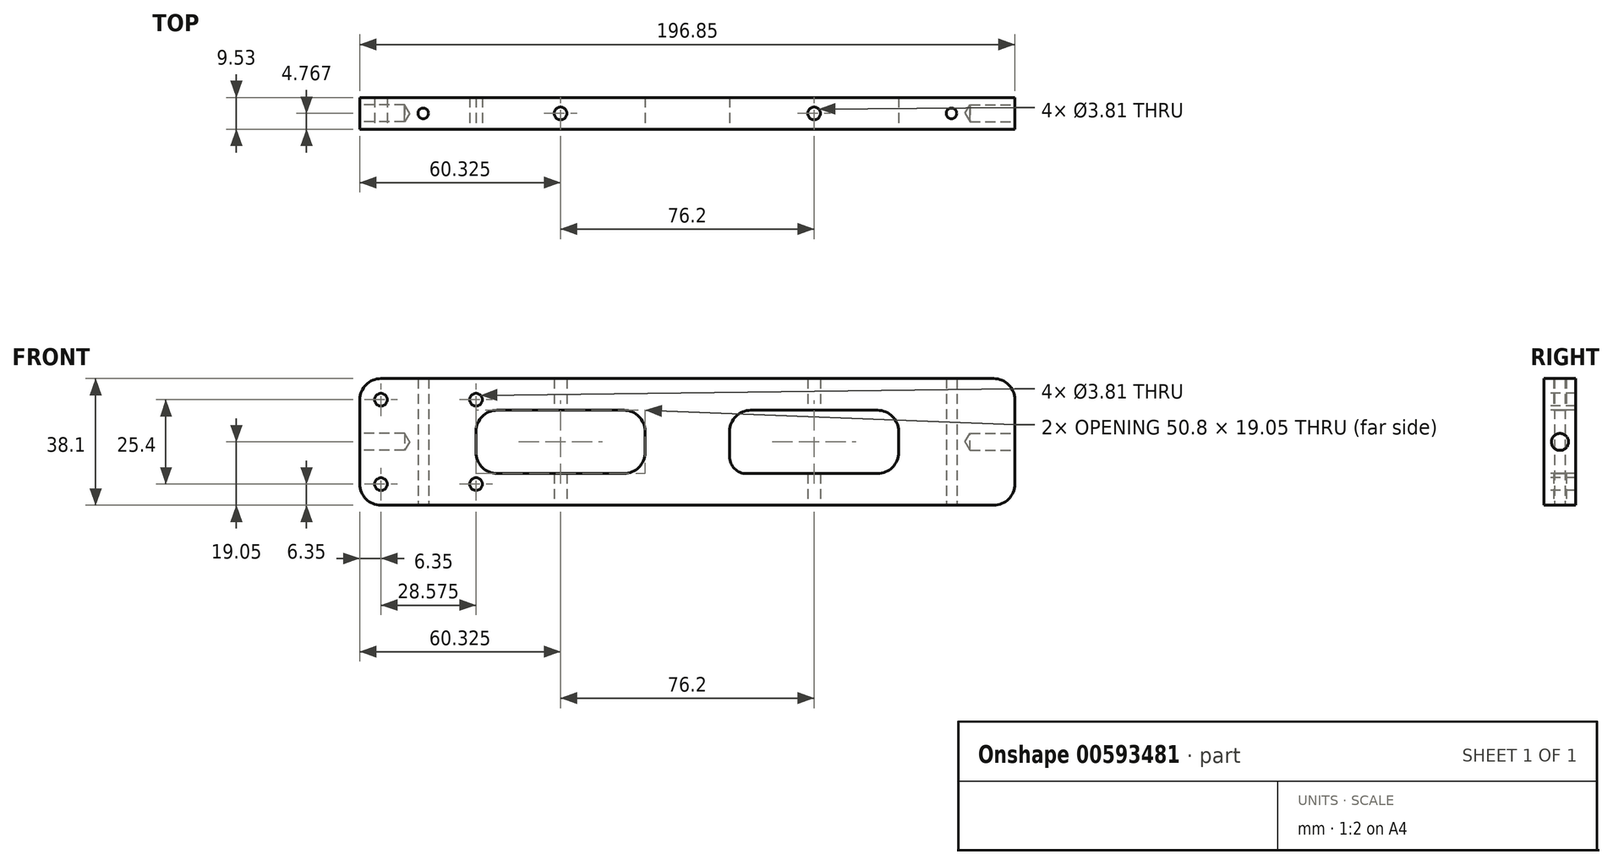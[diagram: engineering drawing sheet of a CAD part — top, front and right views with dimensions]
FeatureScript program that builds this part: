
annotation { "Feature Type Name" : "Feature", "Feature Type Description" : "" }
export const myFeature = defineFeature(function(context is Context, id is Id, definition is map)
    precondition{}
    {
        {
            var Q0;
            Q0=qCreatedBy(makeId("Front.planeOp"),FACE);
            var sketch = newSketch(context, id + "F0", { "sketchPlane" : qUnion([Q0])});
            skLineSegment(sketch, "E0.bottom", {"start": v(-196.85, 47.89) * mm, "end": v(0, 47.89) * mm});
            skLineSegment(sketch, "E0.top", {"start": v(-196.85, 9.79) * mm, "end": v(0, 9.79) * mm});
            skLineSegment(sketch, "E0.left", {"start": v(-196.85, 47.89) * mm, "end": v(-196.85, 9.79) * mm});
            skLineSegment(sketch, "E0.right", {"start": v(0, 47.89) * mm, "end": v(0, 9.79) * mm});
            skSolve(sketch);
        }
        {
            var Q0;
            Q0=makeQuery(id+"F0.imprint","IMPRINT",FACE,{"disambiguationData":[TD([[makeQuery(id+"F0.imprint","IMPRINT",EDGE,{"derivedFrom":sQuery(id+"F0.wireOp",EDGE,"E0.bottom")}),-1.0]])]});
            extrude(context, id + "F1", {"entities" : qUnion([Q0]), "depth" : 9.52 * mm, "offsetDistance" : 25.4 * mm});
        }
        {
            var Q0;
            Q0=makeQuery(id+"F1.opExtrude","SWEPT_EDGE",EDGE,{"disambiguationData":[OSD([sQuery(id+"F0.wireOp",EDGE,"E0.top"),sQuery(id+"F0.wireOp",EDGE,"E0.right")])]});
            fillet(context, id + "F2", {"entities" : qUnion([Q0]), "radius" : 6.35 * mm, "tangentPropagation" : true, "allowEdgeOverflow" : false});
        }
        {
            var Q0;
            Q0=makeQuery(id+"F1.opExtrude","SWEPT_EDGE",EDGE,{"disambiguationData":[OSD([sQuery(id+"F0.wireOp",EDGE,"E0.top"),sQuery(id+"F0.wireOp",EDGE,"E0.left")])]});
            fillet(context, id + "F3", {"entities" : qUnion([Q0]), "radius" : 6.35 * mm, "tangentPropagation" : true, "allowEdgeOverflow" : false});
        }
        {
            var Q0;
            Q0=makeQuery(id+"F1.opExtrude","CAP_FACE",FACE,{"disambiguationData":[OSD([sQuery(id+"F0.wireOp",EDGE,"E0.bottom"),sQuery(id+"F0.wireOp",EDGE,"E0.top"),sQuery(id+"F0.wireOp",EDGE,"E0.left"),sQuery(id+"F0.wireOp",EDGE,"E0.right")])],"isStart":false});
            var sketch = newSketch(context, id + "F4", { "sketchPlane" : qUnion([Q0])});
            skLineSegment(sketch, "E1.bottom", {"start": v(-161.93, 38.36) * mm, "end": v(-111.12, 38.36) * mm});
            skLineSegment(sketch, "E1.top", {"start": v(-161.93, 19.31) * mm, "end": v(-111.12, 19.31) * mm});
            skLineSegment(sketch, "E1.left", {"start": v(-161.93, 38.36) * mm, "end": v(-161.93, 19.31) * mm});
            skLineSegment(sketch, "E1.right", {"start": v(-111.12, 38.36) * mm, "end": v(-111.12, 19.31) * mm});
            skSolve(sketch);
        }
        {
            var Q0;
            Q0 = qSketchRegion(id + "F4", true);
            extrude(context, id + "F5", {"entities" : qUnion([Q0]), "operationType" : NewBodyOperationType.REMOVE, "oppositeDirection" : true, "depth" : 25.4 * mm, "offsetDistance" : 25.4 * mm});
        }
        {
            var Q0;
            Q0=makeQuery(id+"F5.boolean.opBoolean","COPY",EDGE,{"derivedFrom":makeQuery(id+"F5.opExtrude","SWEPT_EDGE",EDGE,{"disambiguationData":[OSD([sQuery(id+"F4.wireOp",EDGE,"E1.bottom"),sQuery(id+"F4.wireOp",EDGE,"E1.left")])]})});
            fillet(context, id + "F6", {"entities" : qUnion([Q0]), "radius" : 6.35 * mm, "tangentPropagation" : true, "allowEdgeOverflow" : false});
        }
        {
            var Q0;
            Q0=makeQuery(id+"F5.boolean.opBoolean","COPY",EDGE,{"derivedFrom":makeQuery(id+"F5.opExtrude","SWEPT_EDGE",EDGE,{"disambiguationData":[OSD([sQuery(id+"F4.wireOp",EDGE,"E1.top"),sQuery(id+"F4.wireOp",EDGE,"E1.left")])]})});
            fillet(context, id + "F7", {"entities" : qUnion([Q0]), "radius" : 6.35 * mm, "tangentPropagation" : true, "allowEdgeOverflow" : false});
        }
        {
            var Q0;
            Q0=makeQuery(id+"F5.boolean.opBoolean","COPY",EDGE,{"derivedFrom":makeQuery(id+"F5.opExtrude","SWEPT_EDGE",EDGE,{"disambiguationData":[OSD([sQuery(id+"F4.wireOp",EDGE,"E1.top"),sQuery(id+"F4.wireOp",EDGE,"E1.right")])]})});
            fillet(context, id + "F8", {"entities" : qUnion([Q0]), "radius" : 6.35 * mm, "tangentPropagation" : true, "allowEdgeOverflow" : false});
        }
        {
            var Q0;
            Q0=makeQuery(id+"F5.boolean.opBoolean","COPY",EDGE,{"derivedFrom":makeQuery(id+"F5.opExtrude","SWEPT_EDGE",EDGE,{"disambiguationData":[OSD([sQuery(id+"F4.wireOp",EDGE,"E1.bottom"),sQuery(id+"F4.wireOp",EDGE,"E1.right")])]})});
            fillet(context, id + "F9", {"entities" : qUnion([Q0]), "radius" : 6.35 * mm, "tangentPropagation" : true, "allowEdgeOverflow" : false});
        }
        {
            var Q0;
            Q0=makeQuery(id+"F1.opExtrude","CAP_FACE",FACE,{"disambiguationData":[OSD([sQuery(id+"F0.wireOp",EDGE,"E0.bottom"),sQuery(id+"F0.wireOp",EDGE,"E0.top"),sQuery(id+"F0.wireOp",EDGE,"E0.left"),sQuery(id+"F0.wireOp",EDGE,"E0.right")])],"isStart":false});
            var sketch = newSketch(context, id + "F10", { "sketchPlane" : qUnion([Q0])});
            skLineSegment(sketch, "E2.bottom", {"start": v(-85.72, 38.36) * mm, "end": v(-34.92, 38.36) * mm});
            skLineSegment(sketch, "E2.top", {"start": v(-85.72, 19.31) * mm, "end": v(-34.92, 19.31) * mm});
            skLineSegment(sketch, "E2.left", {"start": v(-85.72, 38.36) * mm, "end": v(-85.72, 19.31) * mm});
            skLineSegment(sketch, "E2.right", {"start": v(-34.92, 38.36) * mm, "end": v(-34.92, 19.31) * mm});
            skSolve(sketch);
        }
        {
            var Q0;
            Q0 = qSketchRegion(id + "F10", true);
            extrude(context, id + "F11", {"entities" : qUnion([Q0]), "operationType" : NewBodyOperationType.REMOVE, "oppositeDirection" : true, "depth" : 25.4 * mm, "offsetDistance" : 25.4 * mm});
        }
        {
            var Q0;
            Q0=makeQuery(id+"F11.boolean.opBoolean","COPY",EDGE,{"derivedFrom":makeQuery(id+"F11.opExtrude","SWEPT_EDGE",EDGE,{"disambiguationData":[OSD([sQuery(id+"F10.wireOp",EDGE,"E2.bottom"),sQuery(id+"F10.wireOp",EDGE,"E2.left")])]})});
            fillet(context, id + "F12", {"entities" : qUnion([Q0]), "radius" : 6.35 * mm, "tangentPropagation" : true, "allowEdgeOverflow" : false});
        }
        {
            var Q0;
            Q0=makeQuery(id+"F11.boolean.opBoolean","COPY",EDGE,{"derivedFrom":makeQuery(id+"F11.opExtrude","SWEPT_EDGE",EDGE,{"disambiguationData":[OSD([sQuery(id+"F10.wireOp",EDGE,"E2.top"),sQuery(id+"F10.wireOp",EDGE,"E2.left")])]})});
            fillet(context, id + "F13", {"entities" : qUnion([Q0]), "radius" : 5.08 * mm, "tangentPropagation" : true, "allowEdgeOverflow" : false});
        }
        {
            var Q0;
            Q0=makeQuery(id+"F11.boolean.opBoolean","COPY",EDGE,{"derivedFrom":makeQuery(id+"F11.opExtrude","SWEPT_EDGE",EDGE,{"disambiguationData":[OSD([sQuery(id+"F10.wireOp",EDGE,"E2.top"),sQuery(id+"F10.wireOp",EDGE,"E2.right")])]})});
            fillet(context, id + "F14", {"entities" : qUnion([Q0]), "radius" : 6.35 * mm, "tangentPropagation" : true, "allowEdgeOverflow" : false});
        }
        {
            var Q0;
            Q0=makeQuery(id+"F11.boolean.opBoolean","COPY",EDGE,{"derivedFrom":makeQuery(id+"F11.opExtrude","SWEPT_EDGE",EDGE,{"disambiguationData":[OSD([sQuery(id+"F10.wireOp",EDGE,"E2.bottom"),sQuery(id+"F10.wireOp",EDGE,"E2.right")])]})});
            fillet(context, id + "F15", {"entities" : qUnion([Q0]), "radius" : 6.35 * mm, "tangentPropagation" : true, "allowEdgeOverflow" : false});
        }
        {
            var Q0;
            Q0=makeQuery(id+"F1.opExtrude","CAP_FACE",FACE,{"disambiguationData":[OSD([sQuery(id+"F0.wireOp",EDGE,"E0.bottom"),sQuery(id+"F0.wireOp",EDGE,"E0.top"),sQuery(id+"F0.wireOp",EDGE,"E0.left"),sQuery(id+"F0.wireOp",EDGE,"E0.right")])],"isStart":false});
            var sketch = newSketch(context, id + "F16", { "sketchPlane" : qUnion([Q0])});
            skLineSegment(sketch, "E3", {"start": v(-111.12, 47.89) * mm, "end": v(-161.93, 47.89) * mm});
            skCircle(sketch, "E4", {"center": v(-161.93, 16.16) * mm, "radius": 1.9 * mm});
            skCircle(sketch, "E5", {"center": v(-190.5, 16.14) * mm, "radius": 1.9 * mm});
            skCircle(sketch, "E6", {"center": v(-161.93, 41.54) * mm, "radius": 1.9 * mm});
            skCircle(sketch, "E7", {"center": v(-190.5, 41.54) * mm, "radius": 1.9 * mm});
            skSolve(sketch);
        }
        {
            var Q0;
            Q0=makeQuery(id+"F1.opExtrude","SWEPT_FACE",FACE,{"disambiguationData":[OSD([sQuery(id+"F0.wireOp",EDGE,"E0.bottom")])]});
            var sketch = newSketch(context, id + "F17", { "sketchPlane" : qUnion([Q0])});
            skSolve(sketch);
        }
        {
            var Q0;
            Q0=makeQuery(id+"F16.imprint","IMPRINT",FACE,{"disambiguationData":[TD([[makeQuery(id+"F16.imprint","IMPRINT",EDGE,{"derivedFrom":sQuery(id+"F16.wireOp",EDGE,"E7")}),1.0]])]});
            var Q1;
            Q1=makeQuery(id+"F16.imprint","IMPRINT",FACE,{"disambiguationData":[TD([[makeQuery(id+"F16.imprint","IMPRINT",EDGE,{"derivedFrom":sQuery(id+"F16.wireOp",EDGE,"E6")}),1.0]])]});
            var Q2;
            Q2=makeQuery(id+"F16.imprint","IMPRINT",FACE,{"disambiguationData":[TD([[makeQuery(id+"F16.imprint","IMPRINT",EDGE,{"derivedFrom":sQuery(id+"F16.wireOp",EDGE,"E4")}),1.0]])]});
            var Q3;
            Q3=makeQuery(id+"F16.imprint","IMPRINT",FACE,{"disambiguationData":[TD([[makeQuery(id+"F16.imprint","IMPRINT",EDGE,{"derivedFrom":sQuery(id+"F16.wireOp",EDGE,"E5")}),1.0]])]});
            extrude(context, id + "F18", {"entities" : qUnion([Q0, Q1, Q2, Q3]), "operationType" : NewBodyOperationType.REMOVE, "oppositeDirection" : true, "depth" : 25.4 * mm, "offsetDistance" : 25.4 * mm});
        }
        {
            var Q0;
            Q0=makeQuery(id+"F1.opExtrude","SWEPT_FACE",FACE,{"disambiguationData":[OSD([sQuery(id+"F0.wireOp",EDGE,"E0.left")])]});
            var sketch = newSketch(context, id + "F19", { "sketchPlane" : qUnion([Q0])});
            skPoint(sketch, "E8.endSnap0", {"position": v(4.76, 41.54) * mm});
            skPoint(sketch, "E9.endSnap0", {"position": v(4.76, 16.14) * mm});
            skCircle(sketch, "E10", {"center": v(4.76, 28.84) * mm, "radius": 1.9 * mm});
            skSolve(sketch);
        }
        {
            var Q0;
            Q0=makeQuery(id+"F1.opExtrude","SWEPT_FACE",FACE,{"disambiguationData":[OSD([sQuery(id+"F0.wireOp",EDGE,"E0.top")])]});
            var sketch = newSketch(context, id + "F20", { "sketchPlane" : qUnion([Q0])});
            skCircle(sketch, "E11", {"center": v(-177.8, 4.76) * mm, "radius": 1.59 * mm});
            skSolve(sketch);
        }
        {
            var Q0;
            Q0=makeQuery(id+"F20.imprint","IMPRINT",FACE,{"disambiguationData":[TD([[makeQuery(id+"F20.imprint","IMPRINT",EDGE,{"derivedFrom":sQuery(id+"F20.wireOp",EDGE,"E11")}),1.0]])]});
            extrude(context, id + "F21", {"entities" : qUnion([Q0]), "operationType" : NewBodyOperationType.REMOVE, "oppositeDirection" : true, "depth" : 48 * mm, "offsetDistance" : 25.4 * mm});
        }
        {
            var Q0;
            Q0=makeQuery(id+"F1.opExtrude","SWEPT_FACE",FACE,{"disambiguationData":[OSD([sQuery(id+"F0.wireOp",EDGE,"E0.top")])]});
            var sketch = newSketch(context, id + "F22", { "sketchPlane" : qUnion([Q0])});
            skCircle(sketch, "E12", {"center": v(-19.05, 4.76) * mm, "radius": 1.59 * mm});
            skSolve(sketch);
        }
        {
            var Q0;
            Q0=makeQuery(id+"F22.imprint","IMPRINT",FACE,{"disambiguationData":[TD([[makeQuery(id+"F22.imprint","IMPRINT",EDGE,{"derivedFrom":sQuery(id+"F22.wireOp",EDGE,"E12")}),1.0]])]});
            extrude(context, id + "F23", {"entities" : qUnion([Q0]), "operationType" : NewBodyOperationType.REMOVE, "oppositeDirection" : true, "depth" : 44.37 * mm, "offsetDistance" : 25.4 * mm});
        }
        {
            var Q0;
            Q0=makeQuery(id+"F1.opExtrude","SWEPT_FACE",FACE,{"disambiguationData":[OSD([sQuery(id+"F0.wireOp",EDGE,"E0.top")])]});
            var sketch = newSketch(context, id + "F24", { "sketchPlane" : qUnion([Q0])});
            skCircle(sketch, "E13", {"center": v(-60.33, 4.76) * mm, "radius": 1.9 * mm});
            skCircle(sketch, "E14", {"center": v(-136.53, 4.76) * mm, "radius": 1.9 * mm});
            skSolve(sketch);
        }
        {
            var Q0;
            Q0=makeQuery(id+"F1.opExtrude","SWEPT_FACE",FACE,{"disambiguationData":[OSD([sQuery(id+"F0.wireOp",EDGE,"E0.right")])]});
            var sketch = newSketch(context, id + "F25", { "sketchPlane" : qUnion([Q0])});
            skCircle(sketch, "E15", {"center": v(-4.76, 28.84) * mm, "radius": 1.9 * mm});
            skSolve(sketch);
        }
        {
            var Q0;
            Q0=sQuery(id+"F24.wireOp",VERTEX,"E13.center");
            var Q1;
            Q1=sQuery(id+"F24.wireOp",VERTEX,"E14.center");
            var Q2;
            Q2=makeQuery(id+"F1.opExtrude","SWEPT_BODY",BODY,{"disambiguationData":[OSD([sQuery(id+"F0.wireOp",EDGE,"E0.bottom"),sQuery(id+"F0.wireOp",EDGE,"E0.top"),sQuery(id+"F0.wireOp",EDGE,"E0.left"),sQuery(id+"F0.wireOp",EDGE,"E0.right")])]});
            hole(context, id + "F26", {"style" : HoleStyle.SIMPLE, "endStyle" : HoleEndStyle.THROUGH, "holeDiameter" : 3.8 * mm, "majorDiameter" : 6.35 * mm, "isTappedThrough" : true, "tappedDepth" : 12.7 * mm, "tapClearance" : 3, "locations" : qUnion([Q0, Q1]), "scope" : qUnion([Q2])});
        }
        {
            var Q0;
            Q0=sQuery(id+"F25.wireOp",VERTEX,"E15.center");
            var Q1;
            Q1=makeQuery(id+"F1.opExtrude","SWEPT_BODY",BODY,{"disambiguationData":[OSD([sQuery(id+"F0.wireOp",EDGE,"E0.bottom"),sQuery(id+"F0.wireOp",EDGE,"E0.top"),sQuery(id+"F0.wireOp",EDGE,"E0.left"),sQuery(id+"F0.wireOp",EDGE,"E0.right")])]});
            hole(context, id + "F27", {"style" : HoleStyle.SIMPLE, "endStyle" : HoleEndStyle.BLIND, "standardTappedOrClearance" : lookupTablePath({ "standard" : "ANSI", "engagement" : "75%", "pitch" : "20 tpi", "size" : "1/4", "type" : "Tapped" }), "standardBlindInLast" : lookupTablePath({ "standard" : "ANSI", "engagement" : "75%", "pitch" : "20 tpi", "size" : "1/4", "type" : "Tapped" }), "holeDiameter" : 5.1 * mm, "majorDiameter" : 6.35 * mm, "showTappedDepth" : true, "holeDepth" : 13.46 * mm, "tappedDepth" : 9.65 * mm, "tapClearance" : 3, "locations" : qUnion([Q0]), "scope" : qUnion([Q1])});
        }
        {
            var Q0;
            Q0=sQuery(id+"F19.wireOp",VERTEX,"E10.center");
            var Q1;
            Q1=makeQuery(id+"F1.opExtrude","SWEPT_BODY",BODY,{"disambiguationData":[OSD([sQuery(id+"F0.wireOp",EDGE,"E0.bottom"),sQuery(id+"F0.wireOp",EDGE,"E0.top"),sQuery(id+"F0.wireOp",EDGE,"E0.left"),sQuery(id+"F0.wireOp",EDGE,"E0.right")])]});
            hole(context, id + "F28", {"style" : HoleStyle.SIMPLE, "endStyle" : HoleEndStyle.BLIND, "standardTappedOrClearance" : lookupTablePath({ "standard" : "ANSI", "engagement" : "75%", "pitch" : "20 tpi", "size" : "1/4", "type" : "Tapped" }), "standardBlindInLast" : lookupTablePath({ "standard" : "ANSI", "engagement" : "75%", "pitch" : "20 tpi", "size" : "1/4", "type" : "Tapped" }), "holeDiameter" : 5.1 * mm, "majorDiameter" : 6.35 * mm, "showTappedDepth" : true, "holeDepth" : 13.46 * mm, "tappedDepth" : 9.65 * mm, "tapClearance" : 3, "locations" : qUnion([Q0]), "scope" : qUnion([Q1])});
        }
        {
            var Q0;
            Q0=makeQuery(id+"F1.opExtrude","SWEPT_EDGE",EDGE,{"disambiguationData":[OSD([sQuery(id+"F0.wireOp",EDGE,"E0.bottom"),sQuery(id+"F0.wireOp",EDGE,"E0.left")])]});
            var Q1;
            Q1=makeQuery(id+"F1.opExtrude","SWEPT_EDGE",EDGE,{"disambiguationData":[OSD([sQuery(id+"F0.wireOp",EDGE,"E0.bottom"),sQuery(id+"F0.wireOp",EDGE,"E0.right")])]});
            fillet(context, id + "F29", {"entities" : qUnion([Q0, Q1]), "radius" : 6.35 * mm, "tangentPropagation" : true, "allowEdgeOverflow" : false});
        }
    });
